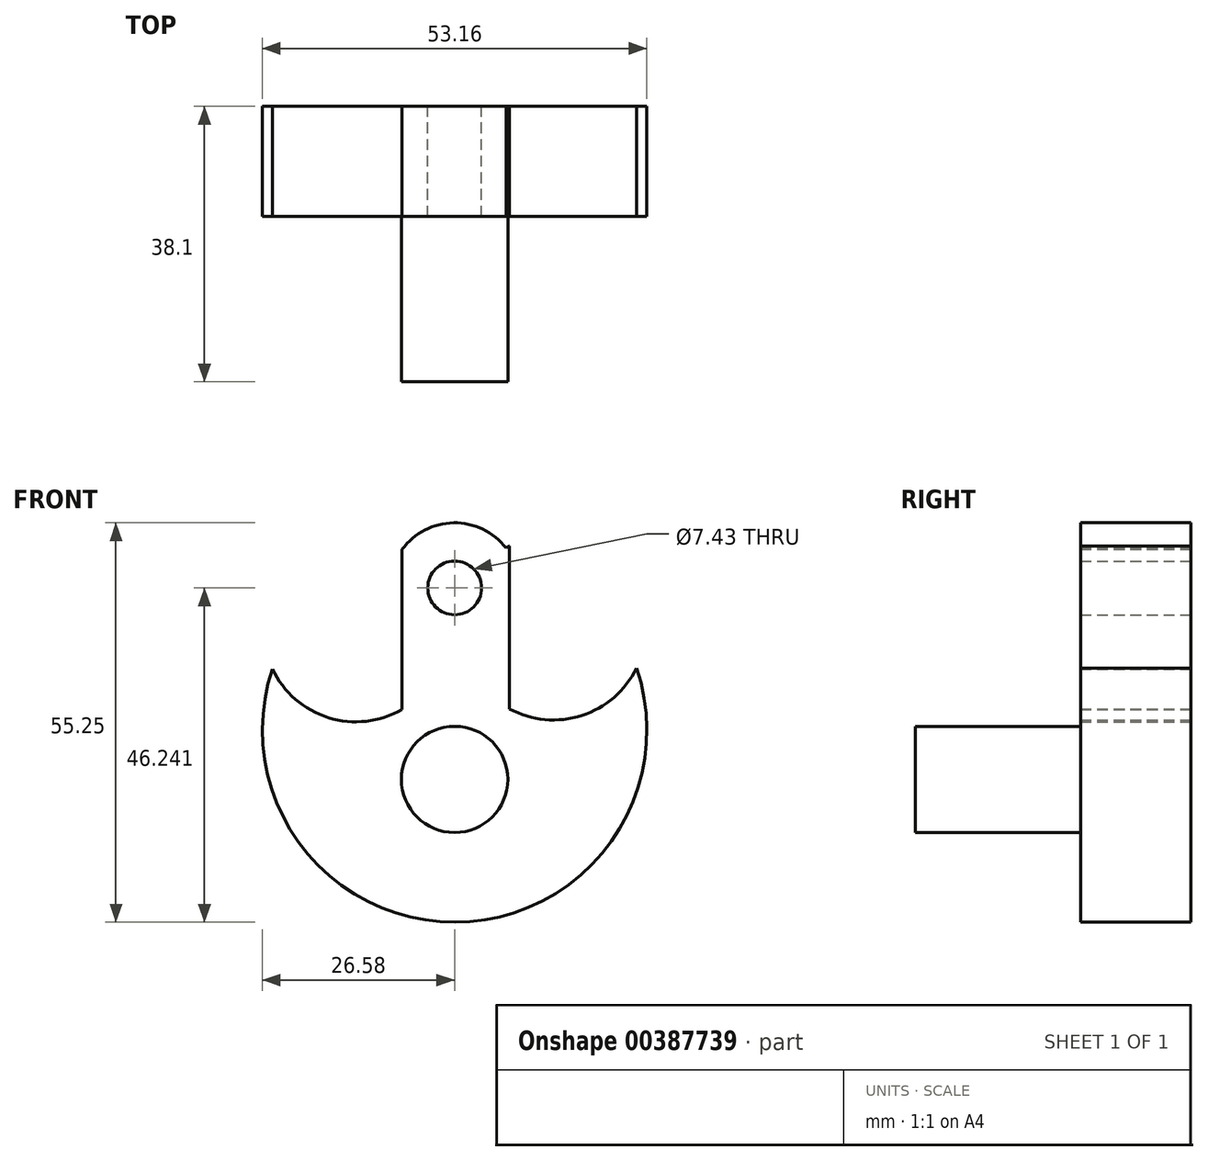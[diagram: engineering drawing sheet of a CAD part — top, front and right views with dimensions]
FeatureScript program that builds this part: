
annotation { "Feature Type Name" : "Feature", "Feature Type Description" : "" }
export const myFeature = defineFeature(function(context is Context, id is Id, definition is map)
    precondition{}
    {
        {
            var Q0;
            Q0=qCreatedBy(makeId("Front.planeOp"),FACE);
            var sketch = newSketch(context, id + "F0", { "sketchPlane" : qUnion([Q0])});
            skArc(sketch, "E0", {"start": v(-25.2, 8.44) * mm, "mid": v(0.07, -26.58) * mm, "end": v(25.15, 8.58) * mm});
            skArc(sketch, "E1", {"start": v(7.59, 25.47) * mm, "mid": v(7.35, 25.34) * mm, "end": v(7.1, 25.2) * mm});
            skArc(sketch, "E2", {"start": v(-25.2, 8.44) * mm, "mid": v(-17.45, 1.72) * mm, "end": v(-7.26, 2.86) * mm});
            skArc(sketch, "E3", {"start": v(7.59, 24.51) * mm, "mid": v(0.3, 28.66) * mm, "end": v(-7.26, 25) * mm});
            skArc(sketch, "E4.trimOffspring", {"start": v(7.59, 2.93) * mm, "mid": v(17.58, 2.02) * mm, "end": v(25.15, 8.58) * mm});
            skArc(sketch, "E5.trimOffspring", {"start": v(-7.26, 25) * mm, "mid": v(-7.6, 25.19) * mm, "end": v(-7.94, 25.36) * mm});
            skLineSegment(sketch, "E6", {"start": v(-7.26, 25) * mm, "end": v(-7.26, 2.86) * mm});
            skLineSegment(sketch, "E7", {"start": v(7.59, 25.47) * mm, "end": v(7.59, 2.93) * mm});
            skCircle(sketch, "E8", {"center": v(0, 19.66) * mm, "radius": 3.71 * mm});
            skCircle(sketch, "E9", {"center": v(0, -6.83) * mm, "radius": 7.35 * mm});
            skSolve(sketch);
        }
        {
            var Q0;
            Q0=qSketchRegion(id+"F0",true);
            extrude(context, id + "F1", {"entities" : qUnion([Q0]), "depth" : 15.24 * mm});
        }
        {
            var Q0;
            Q0=makeQuery(id+"F0.imprint","IMPRINT",FACE,{"disambiguationData":[TD([[makeQuery(id+"F0.imprint","IMPRINT",EDGE,{"derivedFrom":sQuery(id+"F0.wireOp",EDGE,"E9")}),1.0]])]});
            extrude(context, id + "F2", {"entities" : qUnion([Q0]), "operationType" : NewBodyOperationType.ADD, "depth" : 38.1 * mm});
        }
    });
